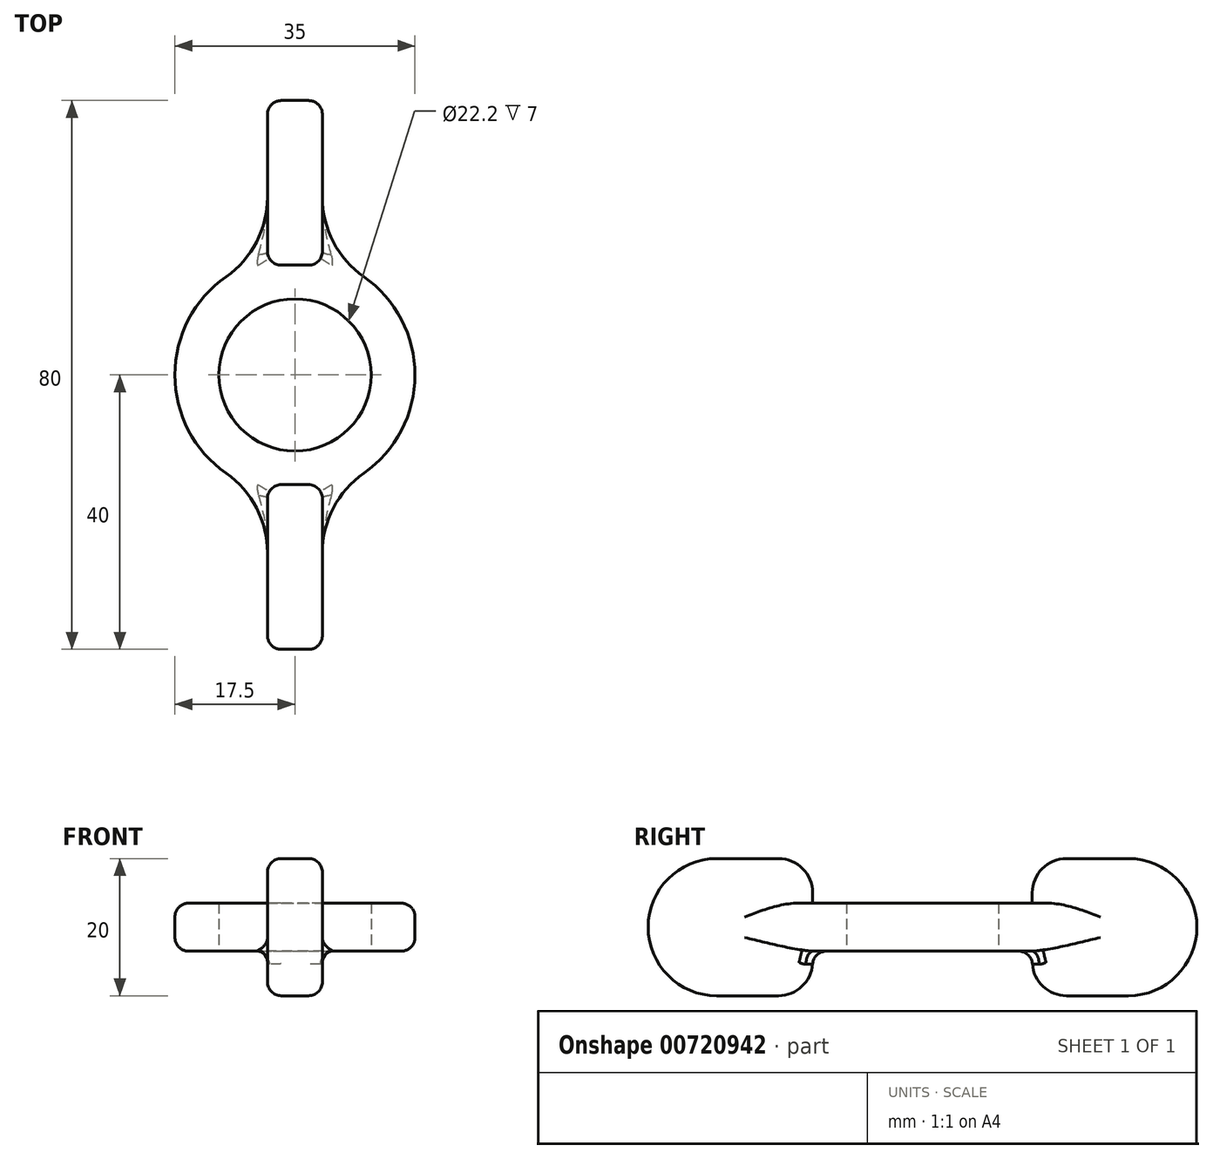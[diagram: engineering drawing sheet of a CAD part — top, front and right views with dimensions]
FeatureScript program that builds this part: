
annotation { "Feature Type Name" : "Feature", "Feature Type Description" : "" }
export const myFeature = defineFeature(function(context is Context, id is Id, definition is map)
    precondition{}
    {
        {
            var Q0;
            Q0=qCreatedBy(makeId("Top.planeOp"),FACE);
            var sketch = newSketch(context, id + "F0", { "sketchPlane" : qUnion([Q0])});
            skCircle(sketch, "E0", {"center": v(0, 0) * mm, "radius": 11.1 * mm});
            skArc(sketch, "E1", {"start": v(-10.04, 14.34) * mm, "mid": v(-15.52, 8.08) * mm, "end": v(-17.5, 0) * mm});
            skArc(sketch, "E2", {"start": v(-10.04, 14.34) * mm, "mid": v(-5.6, 19.4) * mm, "end": v(-4, 25.93) * mm});
            skLineSegment(sketch, "E3", {"start": v(-4, 25.93) * mm, "end": v(-4, 40) * mm});
            skLineSegment(sketch, "E4", {"start": v(-17.5, 0) * mm, "end": v(0, 0) * mm, "construction": true});
            skLineSegment(sketch, "E5", {"start": v(0, 0) * mm, "end": v(0, 40) * mm, "construction": true});
            skArc(sketch, "E6.MirrorCS", {"start": v(10.04, 14.34) * mm, "mid": v(15.52, 8.08) * mm, "end": v(17.5, 0) * mm});
            skArc(sketch, "E7.MirrorCS", {"start": v(10.04, 14.34) * mm, "mid": v(5.6, 19.4) * mm, "end": v(4, 25.93) * mm});
            skLineSegment(sketch, "E8.MirrorCS", {"start": v(4, 25.93) * mm, "end": v(4, 40) * mm});
            skLineSegment(sketch, "E9", {"start": v(-4, 40) * mm, "end": v(4, 40) * mm});
            skLineSegment(sketch, "E10", {"start": v(-10.04, 14.34) * mm, "end": v(0, 0) * mm, "construction": true});
            skLineSegment(sketch, "E11", {"start": v(-4, 25.93) * mm, "end": v(-4, 16) * mm});
            skLineSegment(sketch, "E12", {"start": v(-4, 16) * mm, "end": v(4, 16) * mm});
            skLineSegment(sketch, "E13", {"start": v(4, 16) * mm, "end": v(4, 25.93) * mm});
            skArc(sketch, "E14.MirrorCS", {"start": v(10.04, -14.34) * mm, "mid": v(15.52, -8.08) * mm, "end": v(17.5, 0) * mm});
            skArc(sketch, "E15.MirrorCS", {"start": v(10.04, -14.34) * mm, "mid": v(5.6, -19.4) * mm, "end": v(4, -25.93) * mm});
            skLineSegment(sketch, "E16.MirrorCS", {"start": v(-4, -25.93) * mm, "end": v(-4, -16) * mm});
            skLineSegment(sketch, "E17.MirrorCS", {"start": v(-4, -16) * mm, "end": v(4, -16) * mm});
            skLineSegment(sketch, "E18.MirrorCS", {"start": v(4, -16) * mm, "end": v(4, -25.93) * mm});
            skLineSegment(sketch, "E19.MirrorCS", {"start": v(4, -25.93) * mm, "end": v(4, -40) * mm});
            skLineSegment(sketch, "E20.MirrorCS", {"start": v(-4, -25.93) * mm, "end": v(-4, -40) * mm});
            skLineSegment(sketch, "E21.MirrorCS", {"start": v(-4, -40) * mm, "end": v(4, -40) * mm});
            skArc(sketch, "E22.MirrorCS", {"start": v(-10.04, -14.34) * mm, "mid": v(-5.6, -19.4) * mm, "end": v(-4, -25.93) * mm});
            skArc(sketch, "E23.MirrorCS", {"start": v(-10.04, -14.34) * mm, "mid": v(-15.52, -8.08) * mm, "end": v(-17.5, 0) * mm});
            skSolve(sketch);
        }
        {
            var Q0;
            Q0=makeQuery(id+"F0.imprint","IMPRINT",FACE,{"disambiguationData":[TD([[makeQuery(id+"F0.imprint","IMPRINT",EDGE,{"derivedFrom":sQuery(id+"F0.wireOp",EDGE,"E0")}),-1.0]])]});
            extrude(context, id + "F1", {"entities" : qUnion([Q0]), "endBound" : BoundingType.SYMMETRIC, "depth" : 7 * mm});
        }
        {
            var Q0;
            Q0=makeQuery(id+"F0.imprint","IMPRINT",FACE,{"disambiguationData":[TD([[makeQuery(id+"F0.imprint","IMPRINT",EDGE,{"derivedFrom":sQuery(id+"F0.wireOp",EDGE,"E16.MirrorCS")}),-1.0]])]});
            var Q1;
            Q1=makeQuery(id+"F0.imprint","IMPRINT",FACE,{"disambiguationData":[TD([[makeQuery(id+"F0.imprint","IMPRINT",EDGE,{"derivedFrom":sQuery(id+"F0.wireOp",EDGE,"E3")}),-1.0]])]});
            extrude(context, id + "F2", {"entities" : qUnion([Q0, Q1]), "operationType" : NewBodyOperationType.ADD, "endBound" : BoundingType.SYMMETRIC, "depth" : 20 * mm});
        }
        {
            var Q0;
            Q0=makeQuery(id+"F2.opExtrude","CAP_EDGE",EDGE,{"disambiguationData":[OSD([sQuery(id+"F0.wireOp",EDGE,"E17.MirrorCS")])],"isStart":false});
            var Q1;
            Q1=makeQuery(id+"F2.opExtrude","CAP_EDGE",EDGE,{"disambiguationData":[OSD([sQuery(id+"F0.wireOp",EDGE,"E12")])],"isStart":false});
            var Q2;
            Q2=makeQuery(id+"F2.opExtrude","CAP_EDGE",EDGE,{"disambiguationData":[OSD([sQuery(id+"F0.wireOp",EDGE,"E17.MirrorCS")])],"isStart":true});
            var Q3;
            Q3=makeQuery(id+"F2.opExtrude","CAP_EDGE",EDGE,{"disambiguationData":[OSD([sQuery(id+"F0.wireOp",EDGE,"E12")])],"isStart":true});
            fillet(context, id + "F3", {"entities" : qUnion([Q0, Q1, Q2, Q3]), "radius" : 5 * mm, "tangentPropagation" : true, "allowEdgeOverflow" : false});
        }
        {
            var Q0;
            Q0=makeQuery(id+"F2.opExtrude","CAP_EDGE",EDGE,{"disambiguationData":[OSD([sQuery(id+"F0.wireOp",EDGE,"E21.MirrorCS")])],"isStart":true});
            var Q1;
            Q1=makeQuery(id+"F2.opExtrude","CAP_EDGE",EDGE,{"disambiguationData":[OSD([sQuery(id+"F0.wireOp",EDGE,"E21.MirrorCS")])],"isStart":false});
            var Q2;
            Q2=makeQuery(id+"F2.opExtrude","CAP_EDGE",EDGE,{"disambiguationData":[OSD([sQuery(id+"F0.wireOp",EDGE,"E9")])],"isStart":false});
            var Q3;
            Q3=makeQuery(id+"F2.opExtrude","CAP_EDGE",EDGE,{"disambiguationData":[OSD([sQuery(id+"F0.wireOp",EDGE,"E9")])],"isStart":true});
            fillet(context, id + "F4", {"entities" : qUnion([Q0, Q1, Q2, Q3]), "radius" : 10 * mm, "tangentPropagation" : true, "allowEdgeOverflow" : false});
        }
        {
            var Q0;
            Q0=makeQuery(id+"F2.opExtrude","CAP_EDGE",EDGE,{"disambiguationData":[OSD([sQuery(id+"F0.wireOp",EDGE,"E18.MirrorCS"),sQuery(id+"F0.wireOp",EDGE,"E19.MirrorCS")])],"isStart":false});
            var Q1;
            Q1=makeQuery(id+"F2.opExtrude","CAP_EDGE",EDGE,{"disambiguationData":[OSD([sQuery(id+"F0.wireOp",EDGE,"E16.MirrorCS"),sQuery(id+"F0.wireOp",EDGE,"E20.MirrorCS")])],"isStart":false});
            var Q2;
            Q2=makeQuery(id+"F2.opExtrude","CAP_EDGE",EDGE,{"disambiguationData":[OSD([sQuery(id+"F0.wireOp",EDGE,"E8.MirrorCS"),sQuery(id+"F0.wireOp",EDGE,"E13")])],"isStart":false});
            var Q3;
            Q3=makeQuery(id+"F2.opExtrude","CAP_EDGE",EDGE,{"disambiguationData":[OSD([sQuery(id+"F0.wireOp",EDGE,"E3"),sQuery(id+"F0.wireOp",EDGE,"E11")])],"isStart":false});
            fillet(context, id + "F5", {"entities" : qUnion([Q0, Q1, Q2, Q3]), "radius" : 2 * mm, "tangentPropagation" : true, "allowEdgeOverflow" : false});
        }
        {
            var Q0;
            Q0=makeQuery(id+"F1.opExtrude","CAP_EDGE",EDGE,{"disambiguationData":[OSD([sQuery(id+"F0.wireOp",EDGE,"E6.MirrorCS"),sQuery(id+"F0.wireOp",EDGE,"E14.MirrorCS")])],"isStart":false});
            var Q1;
            Q1=makeQuery(id+"F1.opExtrude","CAP_EDGE",EDGE,{"disambiguationData":[OSD([sQuery(id+"F0.wireOp",EDGE,"E6.MirrorCS"),sQuery(id+"F0.wireOp",EDGE,"E14.MirrorCS")])],"isStart":true});
            var Q2;
            Q2=makeQuery(id+"F1.opExtrude","CAP_EDGE",EDGE,{"disambiguationData":[OSD([sQuery(id+"F0.wireOp",EDGE,"E1"),sQuery(id+"F0.wireOp",EDGE,"E23.MirrorCS")])],"isStart":false});
            var Q3;
            Q3=makeQuery(id+"F1.opExtrude","CAP_EDGE",EDGE,{"disambiguationData":[OSD([sQuery(id+"F0.wireOp",EDGE,"E1"),sQuery(id+"F0.wireOp",EDGE,"E23.MirrorCS")])],"isStart":true});
            fillet(context, id + "F6", {"entities" : qUnion([Q0, Q1, Q2, Q3]), "radius" : 2 * mm, "tangentPropagation" : true, "allowEdgeOverflow" : false});
        }
        {
            var Q0;
            Q0=makeQuery(id+"F1.opExtrude","CAP_EDGE",EDGE,{"disambiguationData":[OSD([sQuery(id+"F0.wireOp",EDGE,"E12")])],"isStart":false});
            var Q1;
            Q1=makeQuery(id+"F1.opExtrude","CAP_EDGE",EDGE,{"disambiguationData":[OSD([sQuery(id+"F0.wireOp",EDGE,"E17.MirrorCS")])],"isStart":false});
            var Q2;
            Q2=makeQuery(id+"F1.opExtrude","CAP_EDGE",EDGE,{"disambiguationData":[OSD([sQuery(id+"F0.wireOp",EDGE,"E17.MirrorCS")])],"isStart":true});
            var Q3;
            Q3=makeQuery(id+"F1.opExtrude","CAP_EDGE",EDGE,{"disambiguationData":[OSD([sQuery(id+"F0.wireOp",EDGE,"E12")])],"isStart":true});
            fillet(context, id + "F7", {"entities" : qUnion([Q0, Q1, Q2, Q3]), "radius" : 2 * mm, "tangentPropagation" : true, "allowEdgeOverflow" : false});
        }
    });
